# Revit family: Roof_Drain_1070_JRSmith
name_source: partatom
category: Plumbing Fixtures
revit_build: Autodesk Revit 2016 (Build: 20150714_1515(x64)
units: mm (PartAtom-declared; Revit-internal decimal feet)

## family parameters
Always vertical = Yes
Cut with Voids When Loaded = No
Part Type = Normal
Room Calculation Point = No
Round Connector Dimension = Use Radius
Shared = No
Work Plane-Based = Yes

## types (6) — shared parameters
04 CSI = 22 14 35
95 CSI = 15165
Assembly Code = D2040200
CW Connection = No
Caulk Connection = Yes
Default Elevation = 0"
Description = Duco cast iron body, flashing clamp and gravel stop with polyethylene dome, PVC standpipe or cast iron water dam
Dome Free Area (Sq. In.) = 102.5
HW Connection = No
Manufacturer = Jay R. Smith Mfg. Co.
Material = Cast Iron
Material Finish = Duco coated
Model = 1070
No-Hub Connection = Yes
OmniClass Code = 22-22 14 26 13
OmniClass Title = Roof Drains
Product URL = http://www.jrsmith.com
Push On Connection = Yes
SMARTBIM Object Version = 3
SMARTBIM URL = www.smartbim.com
Technical and Installation = http://www.jrsmith.com
Threaded Connection = Yes
URL = http://www.jrsmith.com
Vent Connection = No
Warranty = 1 year material and workmanship
Waste Connection = No

## per-type parameters (varying)
| type | Outlet Diameter | Outlet Radius | Weight (lb) |
| 1070-02 | 2" | 1" | 33.12 |
| 1070-03 | 3" | 1 1/2" | 32.55 |
| 1070-04 | 4" | 2" | 31.17 |
| 1070-05 | 5" | 2 1/2" | 31.64 |
| 1070-06 | 6" | 3" | 31.89 |
| 1070-08 | 8" | 4" | 33.12 |

## geometry (parser evidence)
native form markers: Sweep x6
no freeform markers — native parametric forms only
